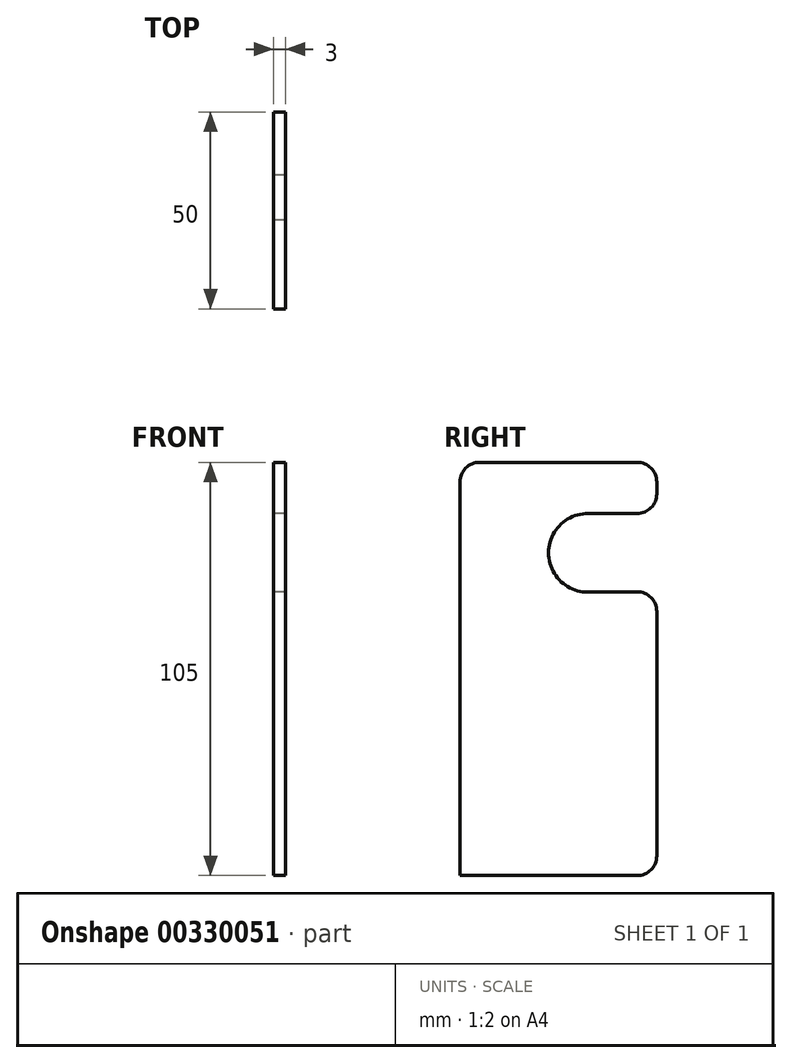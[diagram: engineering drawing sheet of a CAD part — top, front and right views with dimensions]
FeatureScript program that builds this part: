
annotation { "Feature Type Name" : "Feature", "Feature Type Description" : "" }
export const myFeature = defineFeature(function(context is Context, id is Id, definition is map)
    precondition{}
    {
        {
            var Q0;
            Q0=qCreatedBy(makeId("Right.planeOp"),FACE);
            var sketch = newSketch(context, id + "F0", { "sketchPlane" : qUnion([Q0])});
            skLineSegment(sketch, "E0.bottom", {"start": v(-24.55, 52.5) * mm, "end": v(25.45, 52.5) * mm});
            skLineSegment(sketch, "E0.top", {"start": v(-24.55, -52.5) * mm, "end": v(25.45, -52.5) * mm});
            skLineSegment(sketch, "E0.left", {"start": v(-24.55, 52.5) * mm, "end": v(-24.55, -52.5) * mm});
            skLineSegment(sketch, "E0.right", {"start": v(25.45, 52.5) * mm, "end": v(25.45, -52.5) * mm});
            skCircle(sketch, "E1", {"center": v(7.95, 29.5) * mm, "radius": 10 * mm});
            skCircle(sketch, "E2", {"center": v(7.95, 29.5) * mm, "radius": 7.5 * mm});
            skLineSegment(sketch, "E3.bottom", {"start": v(8.03, 39.5) * mm, "end": v(25.45, 39.5) * mm});
            skLineSegment(sketch, "E3.top", {"start": v(8.03, 19.6) * mm, "end": v(25.45, 19.6) * mm});
            skLineSegment(sketch, "E3.left", {"start": v(8.03, 39.5) * mm, "end": v(8.03, 19.6) * mm});
            skLineSegment(sketch, "E3.right", {"start": v(25.45, 39.5) * mm, "end": v(25.45, 19.6) * mm});
            skSolve(sketch);
        }
        {
            var Q0;
            {var subQ1=sQuery(id+"F0.wireOp",EDGE,"E0.bottom");Q0=makeQuery(id+"F0.imprint","IMPRINT",FACE,{"disambiguationData":[TD([[makeQuery(id+"F0.imprint","IMPRINT",EDGE,{"derivedFrom":subQ1}),-1.0]])]});}
            extrude(context, id + "F1", {"entities" : qUnion([Q0]), "depth" : 3 * mm});
        }
        {
            var Q0;
            Q0=makeQuery(id+"F1.opExtrude","SWEPT_EDGE",EDGE,{"disambiguationData":[OSD([sQuery(id+"F0.wireOp",EDGE,"E0.bottom"),sQuery(id+"F0.wireOp",EDGE,"E0.left")])]});
            var Q1;
            Q1=makeQuery(id+"F1.opExtrude","SWEPT_EDGE",EDGE,{"disambiguationData":[OSD([sQuery(id+"F0.wireOp",EDGE,"E0.bottom"),sQuery(id+"F0.wireOp",EDGE,"E0.right")])]});
            var Q2;
            Q2=makeQuery(id+"F1.opExtrude","SWEPT_EDGE",EDGE,{"disambiguationData":[OSD([sQuery(id+"F0.wireOp",EDGE,"E0.right"),sQuery(id+"F0.wireOp",EDGE,"E3.bottom"),sQuery(id+"F0.wireOp",EDGE,"E3.right")])]});
            var Q3;
            Q3=makeQuery(id+"F1.opExtrude","SWEPT_EDGE",EDGE,{"disambiguationData":[OSD([sQuery(id+"F0.wireOp",EDGE,"E0.right"),sQuery(id+"F0.wireOp",EDGE,"E3.top"),sQuery(id+"F0.wireOp",EDGE,"E3.right")])]});
            var Q4;
            Q4=makeQuery(id+"F1.opExtrude","SWEPT_EDGE",EDGE,{"disambiguationData":[OSD([sQuery(id+"F0.wireOp",EDGE,"E0.top"),sQuery(id+"F0.wireOp",EDGE,"E0.right")])]});
            fillet(context, id + "F2", {"entities" : qUnion([Q0, Q1, Q2, Q3, Q4]), "radius" : 5 * mm, "tangentPropagation" : true, "allowEdgeOverflow" : false});
        }
    });
